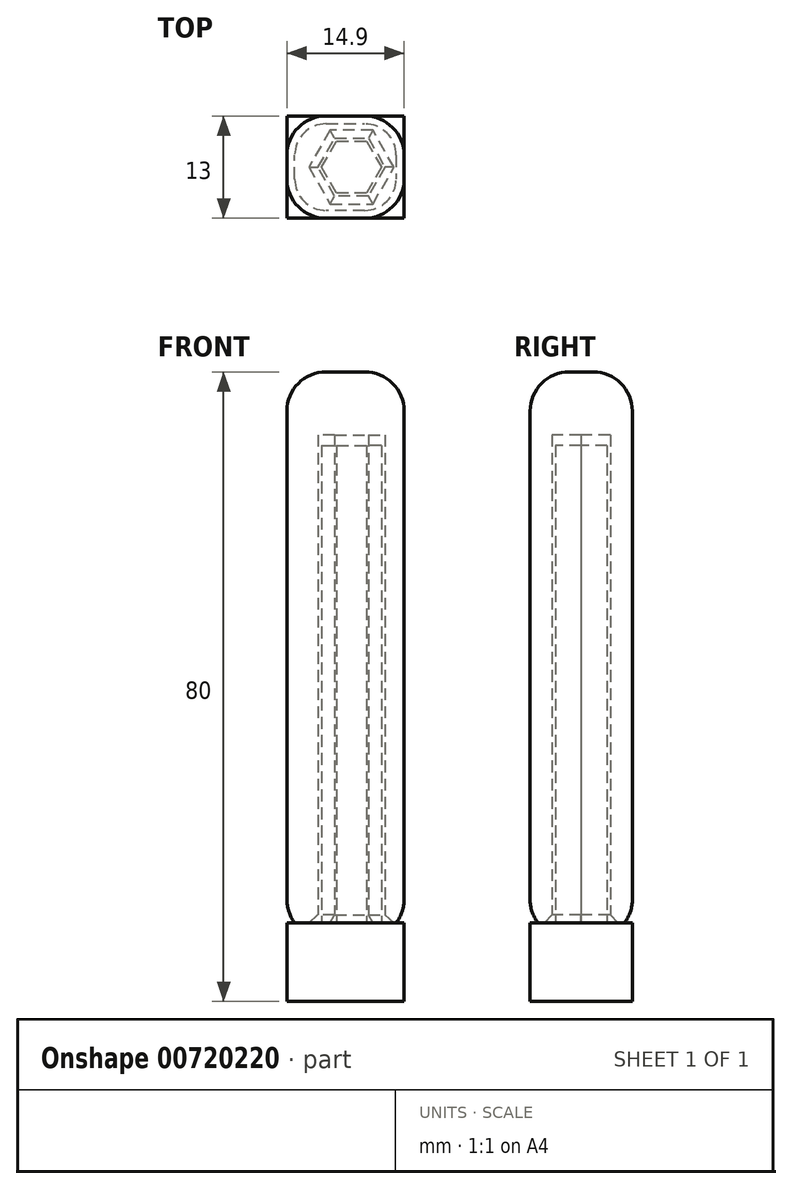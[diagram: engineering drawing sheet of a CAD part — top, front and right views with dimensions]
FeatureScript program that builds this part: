
annotation { "Feature Type Name" : "Feature", "Feature Type Description" : "" }
export const myFeature = defineFeature(function(context is Context, id is Id, definition is map)
    precondition{}
    {
        {
            var Q0;
            Q0=qCreatedBy(makeId("Top.planeOp"),FACE);
            var sketch = newSketch(context, id + "F0", { "sketchPlane" : qUnion([Q0])});
            skCircle(sketch, "E0.cCircle", {"center": v(0, 0) * mm, "radius": 3.8 * mm, "construction": true});
            skLineSegment(sketch, "E0.0", {"start": v(3.8, 0) * mm, "end": v(1.9, -3.3) * mm});
            skLineSegment(sketch, "E0.1", {"start": v(1.9, -3.3) * mm, "end": v(-1.9, -3.3) * mm});
            skLineSegment(sketch, "E0.2", {"start": v(-1.9, -3.3) * mm, "end": v(-3.8, 0) * mm});
            skLineSegment(sketch, "E0.3", {"start": v(-3.8, 0) * mm, "end": v(-1.9, 3.3) * mm});
            skLineSegment(sketch, "E0.4", {"start": v(-1.9, 3.3) * mm, "end": v(1.9, 3.3) * mm});
            skLineSegment(sketch, "E0.5", {"start": v(1.9, 3.3) * mm, "end": v(3.8, 0) * mm});
            skLineSegment(sketch, "E1.bottom", {"start": v(6.68, -6.5) * mm, "end": v(-8.22, -6.5) * mm});
            skLineSegment(sketch, "E1.top", {"start": v(6.68, 6.5) * mm, "end": v(-8.22, 6.5) * mm});
            skLineSegment(sketch, "E1.left", {"start": v(6.68, -6.5) * mm, "end": v(6.68, 6.5) * mm});
            skLineSegment(sketch, "E1.right", {"start": v(-8.22, -6.5) * mm, "end": v(-8.22, 6.5) * mm});
            skPoint(sketch, "E1.middle", {"position": v(-0.77, 0) * mm});
            skLineSegment(sketch, "E2", {"start": v(-0.77, 0) * mm, "end": v(0, 0) * mm, "construction": true});
            skLineSegment(sketch, "E3.0", {"start": v(-2.13, 3.7) * mm, "end": v(2.13, 3.7) * mm});
            skLineSegment(sketch, "E3.1", {"start": v(4.26, 0) * mm, "end": v(2.13, -3.7) * mm});
            skLineSegment(sketch, "E3.2", {"start": v(2.13, -3.7) * mm, "end": v(-2.13, -3.7) * mm});
            skLineSegment(sketch, "E3.3", {"start": v(2.13, 3.7) * mm, "end": v(4.26, 0) * mm});
            skLineSegment(sketch, "E3.4", {"start": v(-2.13, -3.7) * mm, "end": v(-4.26, 0) * mm});
            skLineSegment(sketch, "E3.5", {"start": v(-4.26, 0) * mm, "end": v(-2.13, 3.7) * mm});
            skSolve(sketch);
        }
        {
            var Q0;
            Q0=makeQuery(id+"F0.imprint","IMPRINT",FACE,{"disambiguationData":[TD([[makeQuery(id+"F0.imprint","IMPRINT",EDGE,{"derivedFrom":sQuery(id+"F0.wireOp",EDGE,"E0.0")}),1.0]])]});
            var Q1;
            Q1=makeQuery(id+"F0.imprint","IMPRINT",FACE,{"disambiguationData":[TD([[makeQuery(id+"F0.imprint","IMPRINT",EDGE,{"derivedFrom":sQuery(id+"F0.wireOp",EDGE,"E0.0")}),-1.0]])]});
            var Q2;
            Q2=makeQuery(id+"F0.imprint","IMPRINT",FACE,{"disambiguationData":[TD([[makeQuery(id+"F0.imprint","IMPRINT",EDGE,{"derivedFrom":sQuery(id+"F0.wireOp",EDGE,"E1.bottom")}),-1.0]])]});
            extrude(context, id + "F1", {"entities" : qUnion([Q0, Q1, Q2]), "oppositeDirection" : true, "depth" : 10 * mm, "offsetDistance" : 25 * mm});
        }
        {
            var Q0;
            Q0=makeQuery(id+"F0.imprint","IMPRINT",FACE,{"disambiguationData":[TD([[makeQuery(id+"F0.imprint","IMPRINT",EDGE,{"derivedFrom":sQuery(id+"F0.wireOp",EDGE,"E0.0")}),-1.0]])]});
            extrude(context, id + "F2", {"entities" : qUnion([Q0]), "operationType" : NewBodyOperationType.ADD, "depth" : 60.65 * mm, "offsetDistance" : 25 * mm});
        }
        {
            var Q0;
            Q0=makeQuery(id+"F0.imprint","IMPRINT",FACE,{"disambiguationData":[TD([[makeQuery(id+"F0.imprint","IMPRINT",EDGE,{"derivedFrom":sQuery(id+"F0.wireOp",EDGE,"E1.bottom")}),-1.0]])]});
            extrude(context, id + "F3", {"entities" : qUnion([Q0]), "depth" : 70 * mm, "offsetDistance" : 25 * mm});
        }
        {
            var Q0;
            Q0=makeQuery(id+"F3.opExtrude","CAP_FACE",FACE,{"disambiguationData":[OSD([sQuery(id+"F0.wireOp",EDGE,"E1.bottom"),sQuery(id+"F0.wireOp",EDGE,"E1.top"),sQuery(id+"F0.wireOp",EDGE,"E1.left"),sQuery(id+"F0.wireOp",EDGE,"E1.right"),sQuery(id+"F0.wireOp",EDGE,"E3.0"),sQuery(id+"F0.wireOp",EDGE,"E3.1"),sQuery(id+"F0.wireOp",EDGE,"E3.2"),sQuery(id+"F0.wireOp",EDGE,"E3.3"),sQuery(id+"F0.wireOp",EDGE,"E3.4"),sQuery(id+"F0.wireOp",EDGE,"E3.5")])],"isStart":false});
            var sketch = newSketch(context, id + "F4", { "sketchPlane" : qUnion([Q0])});
            skCircle(sketch, "E4.cCircle", {"center": v(0, 0) * mm, "radius": 3.8 * mm, "construction": true});
            skLineSegment(sketch, "E4.0", {"start": v(3.8, 0) * mm, "end": v(1.9, -3.3) * mm});
            skLineSegment(sketch, "E4.1", {"start": v(1.9, -3.3) * mm, "end": v(-1.9, -3.3) * mm});
            skLineSegment(sketch, "E4.2", {"start": v(-1.9, -3.3) * mm, "end": v(-3.8, 0) * mm});
            skLineSegment(sketch, "E4.3", {"start": v(-3.8, 0) * mm, "end": v(-1.9, 3.3) * mm});
            skLineSegment(sketch, "E4.4", {"start": v(-1.9, 3.3) * mm, "end": v(1.9, 3.3) * mm});
            skLineSegment(sketch, "E4.5", {"start": v(1.9, 3.3) * mm, "end": v(3.8, 0) * mm});
            skLineSegment(sketch, "E5.bottom", {"start": v(6.68, -6.5) * mm, "end": v(-8.22, -6.5) * mm});
            skLineSegment(sketch, "E5.top", {"start": v(6.68, 6.5) * mm, "end": v(-8.22, 6.5) * mm});
            skLineSegment(sketch, "E5.left", {"start": v(6.68, -6.5) * mm, "end": v(6.68, 6.5) * mm});
            skLineSegment(sketch, "E5.right", {"start": v(-8.22, -6.5) * mm, "end": v(-8.22, 6.5) * mm});
            skPoint(sketch, "E5.middle", {"position": v(-0.77, 0) * mm});
            skLineSegment(sketch, "E6", {"start": v(-0.77, 0) * mm, "end": v(0, 0) * mm, "construction": true});
            skLineSegment(sketch, "E7.0", {"start": v(-2.13, 3.7) * mm, "end": v(2.13, 3.7) * mm});
            skLineSegment(sketch, "E7.1", {"start": v(4.26, 0) * mm, "end": v(2.13, -3.7) * mm});
            skLineSegment(sketch, "E7.2", {"start": v(2.13, -3.7) * mm, "end": v(-2.13, -3.7) * mm});
            skLineSegment(sketch, "E7.3", {"start": v(2.13, 3.7) * mm, "end": v(4.26, 0) * mm});
            skLineSegment(sketch, "E7.4", {"start": v(-2.13, -3.7) * mm, "end": v(-4.26, 0) * mm});
            skLineSegment(sketch, "E7.5", {"start": v(-4.26, 0) * mm, "end": v(-2.13, 3.7) * mm});
            skLineSegment(sketch, "E8", {"start": v(0, 0) * mm, "end": v(4.26, 0) * mm, "construction": true});
            skSolve(sketch);
        }
        {
            var Q0;
            Q0=makeQuery(id+"F4.imprint","IMPRINT",FACE,{"disambiguationData":[TD([[makeQuery(id+"F4.imprint","IMPRINT",EDGE,{"derivedFrom":sQuery(id+"F4.wireOp",EDGE,"E4.0")}),-1.0]])]});
            var Q1;
            Q1=makeQuery(id+"F4.imprint","IMPRINT",FACE,{"disambiguationData":[TD([[makeQuery(id+"F4.imprint","IMPRINT",EDGE,{"derivedFrom":sQuery(id+"F4.wireOp",EDGE,"E4.0")}),1.0]])]});
            extrude(context, id + "F5", {"entities" : qUnion([Q0, Q1]), "operationType" : NewBodyOperationType.ADD, "oppositeDirection" : true, "depth" : 8 * mm, "offsetDistance" : 25 * mm});
        }
        {
            var Q0;
            Q0=makeQuery(id+"F3.opExtrude","CAP_FACE",FACE,{"disambiguationData":[OSD([sQuery(id+"F0.wireOp",EDGE,"E1.bottom"),sQuery(id+"F0.wireOp",EDGE,"E1.top"),sQuery(id+"F0.wireOp",EDGE,"E1.left"),sQuery(id+"F0.wireOp",EDGE,"E1.right"),sQuery(id+"F0.wireOp",EDGE,"E3.0"),sQuery(id+"F0.wireOp",EDGE,"E3.1"),sQuery(id+"F0.wireOp",EDGE,"E3.2"),sQuery(id+"F0.wireOp",EDGE,"E3.3"),sQuery(id+"F0.wireOp",EDGE,"E3.4"),sQuery(id+"F0.wireOp",EDGE,"E3.5")])],"isStart":true});
            chamfer(context, id + "F6", {"entities" : qUnion([Q0]), "width" : 1 * mm, "tangentPropagation" : true});
        }
        {
            var Q0;
            {var subQ0=sQuery(id+"F0.wireOp",EDGE,"E1.right");Q0=makeQuery(id+"F6.opChamfer","BLEND_EDGE",EDGE,{"blendedFrom":[makeQuery(id+"F3.opExtrude","CAP_EDGE",EDGE,{"disambiguationData":[OSD([subQ0])],"isStart":true}),makeQuery(id+"F3.opExtrude","SWEPT_FACE",FACE,{"disambiguationData":[OSD([subQ0])]})],"blendedInto":[makeQuery(id+"F3.opExtrude","SWEPT_FACE",FACE,{"disambiguationData":[OSD([subQ0])]})]});}
            var Q1;
            {var subQ0=sQuery(id+"F0.wireOp",EDGE,"E1.top");Q1=makeQuery(id+"F6.opChamfer","BLEND_EDGE",EDGE,{"blendedFrom":[makeQuery(id+"F3.opExtrude","CAP_EDGE",EDGE,{"disambiguationData":[OSD([subQ0])],"isStart":true}),makeQuery(id+"F3.opExtrude","SWEPT_FACE",FACE,{"disambiguationData":[OSD([subQ0])]})],"blendedInto":[makeQuery(id+"F3.opExtrude","SWEPT_FACE",FACE,{"disambiguationData":[OSD([subQ0])]})]});}
            var Q2;
            {var subQ0=sQuery(id+"F0.wireOp",EDGE,"E1.left");Q2=makeQuery(id+"F6.opChamfer","BLEND_EDGE",EDGE,{"blendedFrom":[makeQuery(id+"F3.opExtrude","CAP_EDGE",EDGE,{"disambiguationData":[OSD([subQ0])],"isStart":true}),makeQuery(id+"F3.opExtrude","SWEPT_FACE",FACE,{"disambiguationData":[OSD([subQ0])]})],"blendedInto":[makeQuery(id+"F3.opExtrude","SWEPT_FACE",FACE,{"disambiguationData":[OSD([subQ0])]})]});}
            var Q3;
            {var subQ0=sQuery(id+"F0.wireOp",EDGE,"E1.bottom");Q3=makeQuery(id+"F6.opChamfer","BLEND_EDGE",EDGE,{"blendedFrom":[makeQuery(id+"F3.opExtrude","CAP_EDGE",EDGE,{"disambiguationData":[OSD([subQ0])],"isStart":true}),makeQuery(id+"F3.opExtrude","SWEPT_FACE",FACE,{"disambiguationData":[OSD([subQ0])]})],"blendedInto":[makeQuery(id+"F3.opExtrude","SWEPT_FACE",FACE,{"disambiguationData":[OSD([subQ0])]})]});}
            fillet(context, id + "F7", {"entities" : qUnion([Q0, Q1, Q2, Q3]), "radius" : 5 * mm, "tangentPropagation" : true, "allowEdgeOverflow" : false});
        }
        {
            var Q0;
            Q0=makeQuery(id+"F3.opExtrude","SWEPT_EDGE",EDGE,{"disambiguationData":[OSD([sQuery(id+"F0.wireOp",EDGE,"E1.top"),sQuery(id+"F0.wireOp",EDGE,"E1.right")])]});
            var Q1;
            Q1=makeQuery(id+"F3.opExtrude","SWEPT_EDGE",EDGE,{"disambiguationData":[OSD([sQuery(id+"F0.wireOp",EDGE,"E1.top"),sQuery(id+"F0.wireOp",EDGE,"E1.left")])]});
            var Q2;
            Q2=makeQuery(id+"F3.opExtrude","SWEPT_EDGE",EDGE,{"disambiguationData":[OSD([sQuery(id+"F0.wireOp",EDGE,"E1.bottom"),sQuery(id+"F0.wireOp",EDGE,"E1.left")])]});
            var Q3;
            Q3=makeQuery(id+"F3.opExtrude","SWEPT_EDGE",EDGE,{"disambiguationData":[OSD([sQuery(id+"F0.wireOp",EDGE,"E1.bottom"),sQuery(id+"F0.wireOp",EDGE,"E1.right")])]});
            fillet(context, id + "F8", {"entities" : qUnion([Q0, Q1, Q2, Q3]), "radius" : 5 * mm, "tangentPropagation" : true, "allowEdgeOverflow" : false});
        }
        {
            var Q0;
            Q0=makeQuery(id+"F5.boolean.opBoolean","MERGE",FACE,{"derivedFrom":[makeQuery(id+"F3.opExtrude","CAP_FACE",FACE,{"disambiguationData":[OSD([sQuery(id+"F0.wireOp",EDGE,"E1.bottom"),sQuery(id+"F0.wireOp",EDGE,"E1.top"),sQuery(id+"F0.wireOp",EDGE,"E1.left"),sQuery(id+"F0.wireOp",EDGE,"E1.right"),sQuery(id+"F0.wireOp",EDGE,"E3.0"),sQuery(id+"F0.wireOp",EDGE,"E3.1"),sQuery(id+"F0.wireOp",EDGE,"E3.2"),sQuery(id+"F0.wireOp",EDGE,"E3.3"),sQuery(id+"F0.wireOp",EDGE,"E3.4"),sQuery(id+"F0.wireOp",EDGE,"E3.5")])],"isStart":false}),makeQuery(id+"F5.opExtrude","CAP_FACE",FACE,{"disambiguationData":[OSD([sQuery(id+"F4.wireOp",EDGE,"E7.0"),sQuery(id+"F4.wireOp",EDGE,"E7.1"),sQuery(id+"F4.wireOp",EDGE,"E7.2"),sQuery(id+"F4.wireOp",EDGE,"E7.3"),sQuery(id+"F4.wireOp",EDGE,"E7.4"),sQuery(id+"F4.wireOp",EDGE,"E7.5")])],"isStart":true})]});
            fillet(context, id + "F9", {"entities" : qUnion([Q0]), "radius" : 5 * mm, "tangentPropagation" : true, "allowEdgeOverflow" : false});
        }
    });
